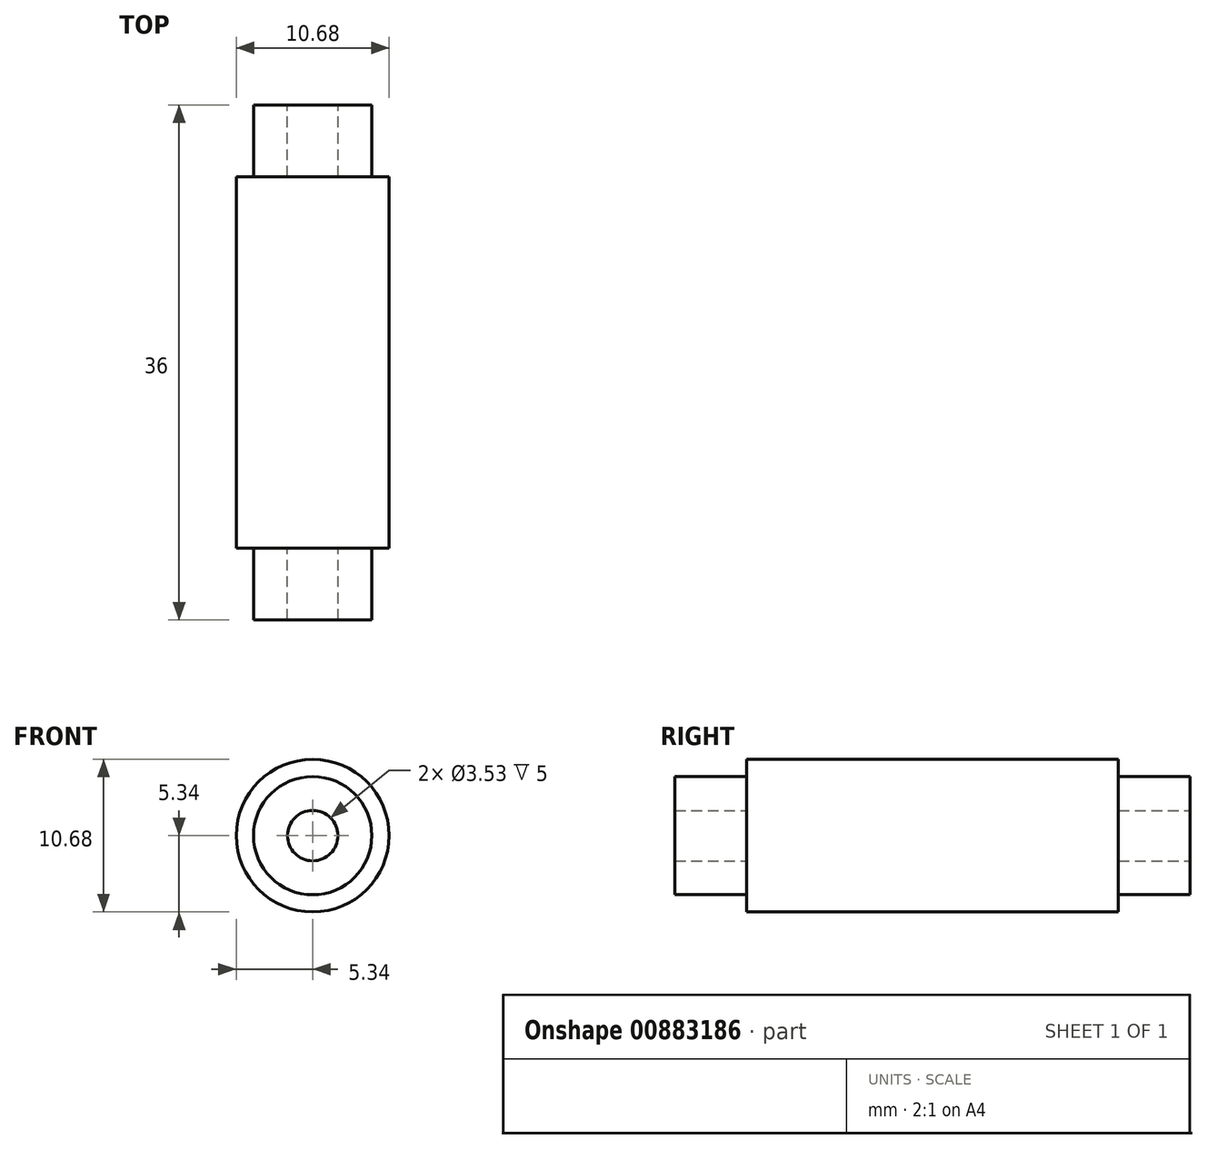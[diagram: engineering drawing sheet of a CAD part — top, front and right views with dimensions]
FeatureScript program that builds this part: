
annotation { "Feature Type Name" : "Feature", "Feature Type Description" : "" }
export const myFeature = defineFeature(function(context is Context, id is Id, definition is map)
    precondition{}
    {
        {
            var Q0;
            Q0=qCreatedBy(makeId("Front.planeOp"),FACE);
            var sketch = newSketch(context, id + "F0", { "sketchPlane" : qUnion([Q0])});
            skCircle(sketch, "E0", {"center": v(0, 0) * mm, "radius": 1.77 * mm});
            skCircle(sketch, "E1", {"center": v(0, 0) * mm, "radius": 4.13 * mm});
            skSolve(sketch);
        }
        {
            var Q0;
            Q0=makeQuery(id+"F0.imprint","IMPRINT",FACE,{"disambiguationData":[TD([[makeQuery(id+"F0.imprint","IMPRINT",EDGE,{"derivedFrom":sQuery(id+"F0.wireOp",EDGE,"E0")}),-1.0]])]});
            extrude(context, id + "F1", {"entities" : qUnion([Q0]), "depth" : 36 * mm, "offsetDistance" : 25 * mm});
        }
        {
            var Q0;
            Q0=makeQuery(id+"F0.imprint","IMPRINT",FACE,{"disambiguationData":[TD([[makeQuery(id+"F0.imprint","IMPRINT",EDGE,{"derivedFrom":sQuery(id+"F0.wireOp",EDGE,"E0")}),-1.0]])]});
            cPlane(context, id + "F2", {"entities" : qUnion([Q0]), "cplaneType" : CPlaneType.OFFSET, "offset" : 5 * mm, "width" : 150 * mm, "height" : 150 * mm});
        }
        {
            var Q0;
            Q0=qCreatedBy(id+"F2.planeOp",FACE);
            var sketch = newSketch(context, id + "F3", { "sketchPlane" : qUnion([Q0])});
            skCircle(sketch, "E2", {"center": v(0, 0) * mm, "radius": 5.33 * mm});
            skSolve(sketch);
        }
        {
            var Q0;
            Q0 = qSketchRegion(id + "F3", true);
            extrude(context, id + "F4", {"entities" : qUnion([Q0]), "operationType" : NewBodyOperationType.ADD, "depth" : 26 * mm, "offsetDistance" : 25 * mm});
        }
    });
